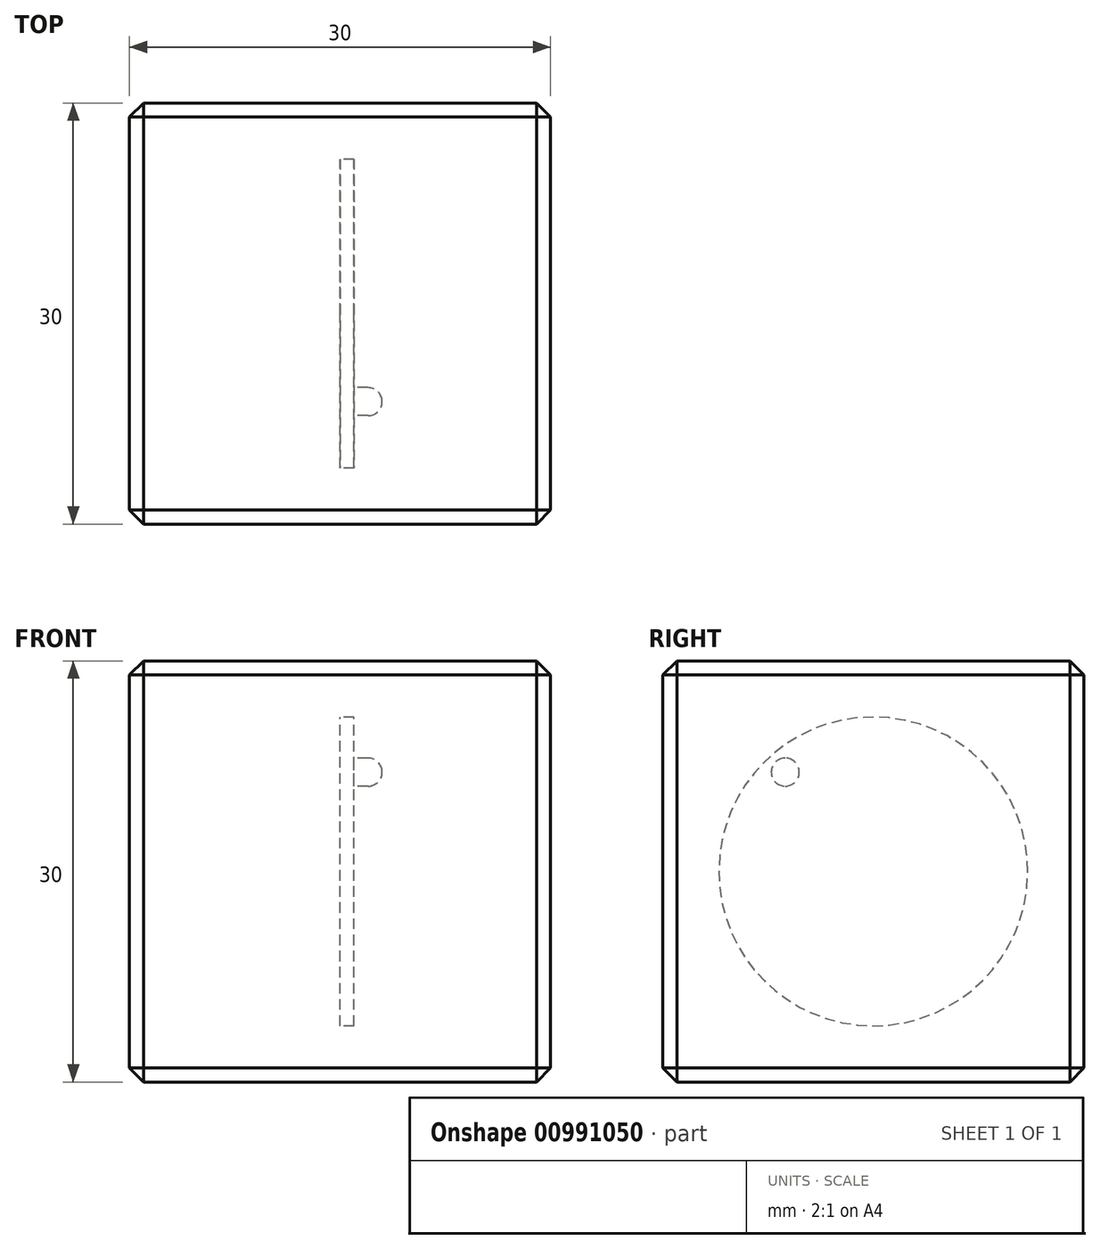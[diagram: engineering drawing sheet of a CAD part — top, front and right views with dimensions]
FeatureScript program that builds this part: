
annotation { "Feature Type Name" : "Feature", "Feature Type Description" : "" }
export const myFeature = defineFeature(function(context is Context, id is Id, definition is map)
    precondition{}
    {
        {
            var Q0;
            Q0=qCreatedBy(makeId("Right.planeOp"),FACE);
            var sketch = newSketch(context, id + "F0", { "sketchPlane" : qUnion([Q0])});
            skCircle(sketch, "E0", {"center": v(0, 0) * mm, "radius": 11 * mm});
            skSolve(sketch);
        }
        {
            var Q0;
            Q0=makeQuery(id+"F0.imprint","IMPRINT",FACE,{"disambiguationData":[TD([[makeQuery(id+"F0.imprint","IMPRINT",EDGE,{"derivedFrom":sQuery(id+"F0.wireOp",EDGE,"E0")}),1.0]])]});
            extrude(context, id + "F1", {"entities" : qUnion([Q0]), "depth" : 1 * mm, "offsetDistance" : 25 * mm});
        }
        {
            var Q0;
            Q0=makeQuery(id+"F1.opExtrude","CAP_FACE",FACE,{"disambiguationData":[OSD([sQuery(id+"F0.wireOp",EDGE,"E0")])],"isStart":false});
            var sketch = newSketch(context, id + "F2", { "sketchPlane" : qUnion([Q0])});
            skCircle(sketch, "E1", {"center": v(-6.28, 7.07) * mm, "radius": 1 * mm});
            skSolve(sketch);
        }
        {
            var Q0;
            Q0=makeQuery(id+"F2.imprint","IMPRINT",FACE,{"disambiguationData":[TD([[makeQuery(id+"F2.imprint","IMPRINT",EDGE,{"derivedFrom":sQuery(id+"F2.wireOp",EDGE,"E1")}),1.0]])]});
            var Q1;
            Q1=sQuery(id+"F2.wireOp",EDGE,"E1");
            extrude(context, id + "F3", {"entities" : qUnion([Q0]), "operationType" : NewBodyOperationType.ADD, "surfaceEntities" : qUnion([Q1]), "depth" : 2 * mm, "offsetDistance" : 25 * mm});
        }
        {
            var Q0;
            Q0=makeQuery(id+"F3.opExtrude","CAP_EDGE",EDGE,{"disambiguationData":[OSD([sQuery(id+"F2.wireOp",EDGE,"E1")])],"isStart":false});
            fillet(context, id + "F4", {"entities" : qUnion([Q0]), "radius" : 1 * mm, "tangentPropagation" : true, "allowEdgeOverflow" : false});
        }
        {
            var Q0;
            Q0=qCreatedBy(makeId("Right.planeOp"),FACE);
            var sketch = newSketch(context, id + "F5", { "sketchPlane" : qUnion([Q0])});
            skLineSegment(sketch, "E2.bottom", {"start": v(-15, -15) * mm, "end": v(15, -15) * mm});
            skLineSegment(sketch, "E2.top", {"start": v(-15, 15) * mm, "end": v(15, 15) * mm});
            skLineSegment(sketch, "E2.left", {"start": v(-15, -15) * mm, "end": v(-15, 15) * mm});
            skLineSegment(sketch, "E2.right", {"start": v(15, -15) * mm, "end": v(15, 15) * mm});
            skSolve(sketch);
        }
        {
            var Q0;
            Q0=makeQuery(id+"F5.imprint","IMPRINT",FACE,{"disambiguationData":[TD([[makeQuery(id+"F5.imprint","IMPRINT",EDGE,{"derivedFrom":sQuery(id+"F5.wireOp",EDGE,"E2.bottom")}),1.0]])]});
            extrude(context, id + "F6", {"entities" : qUnion([Q0]), "endBound" : BoundingType.SYMMETRIC, "depth" : 30 * mm, "offsetDistance" : 25 * mm});
        }
        {
            var Q0;
            Q0=makeQuery(id+"F6.opExtrude","SWEPT_EDGE",EDGE,{"disambiguationData":[OSD([sQuery(id+"F5.wireOp",EDGE,"E2.bottom"),sQuery(id+"F5.wireOp",EDGE,"E2.left")])]});
            var Q1;
            Q1=makeQuery(id+"F6.opExtrude","CAP_EDGE",EDGE,{"disambiguationData":[OSD([sQuery(id+"F5.wireOp",EDGE,"E2.left")])],"isStart":false});
            var Q2;
            Q2=makeQuery(id+"F6.opExtrude","SWEPT_EDGE",EDGE,{"disambiguationData":[OSD([sQuery(id+"F5.wireOp",EDGE,"E2.top"),sQuery(id+"F5.wireOp",EDGE,"E2.left")])]});
            var Q3;
            Q3=makeQuery(id+"F6.opExtrude","CAP_EDGE",EDGE,{"disambiguationData":[OSD([sQuery(id+"F5.wireOp",EDGE,"E2.left")])],"isStart":true});
            var Q4;
            Q4=makeQuery(id+"F6.opExtrude","CAP_EDGE",EDGE,{"disambiguationData":[OSD([sQuery(id+"F5.wireOp",EDGE,"E2.bottom")])],"isStart":true});
            var Q5;
            Q5=makeQuery(id+"F6.opExtrude","CAP_EDGE",EDGE,{"disambiguationData":[OSD([sQuery(id+"F5.wireOp",EDGE,"E2.bottom")])],"isStart":false});
            var Q6;
            Q6=makeQuery(id+"F6.opExtrude","SWEPT_EDGE",EDGE,{"disambiguationData":[OSD([sQuery(id+"F5.wireOp",EDGE,"E2.bottom"),sQuery(id+"F5.wireOp",EDGE,"E2.right")])]});
            var Q7;
            Q7=makeQuery(id+"F6.opExtrude","CAP_EDGE",EDGE,{"disambiguationData":[OSD([sQuery(id+"F5.wireOp",EDGE,"E2.right")])],"isStart":false});
            var Q8;
            Q8=makeQuery(id+"F6.opExtrude","CAP_EDGE",EDGE,{"disambiguationData":[OSD([sQuery(id+"F5.wireOp",EDGE,"E2.top")])],"isStart":false});
            var Q9;
            Q9=makeQuery(id+"F6.opExtrude","SWEPT_EDGE",EDGE,{"disambiguationData":[OSD([sQuery(id+"F5.wireOp",EDGE,"E2.top"),sQuery(id+"F5.wireOp",EDGE,"E2.right")])]});
            var Q10;
            Q10=makeQuery(id+"F6.opExtrude","CAP_EDGE",EDGE,{"disambiguationData":[OSD([sQuery(id+"F5.wireOp",EDGE,"E2.top")])],"isStart":true});
            var Q11;
            Q11=makeQuery(id+"F6.opExtrude","CAP_EDGE",EDGE,{"disambiguationData":[OSD([sQuery(id+"F5.wireOp",EDGE,"E2.right")])],"isStart":true});
            chamfer(context, id + "F7", {"entities" : qUnion([Q0, Q1, Q2, Q3, Q4, Q5, Q6, Q7, Q8, Q9, Q10, Q11]), "width" : 1 * mm, "tangentPropagation" : true});
        }
    });
